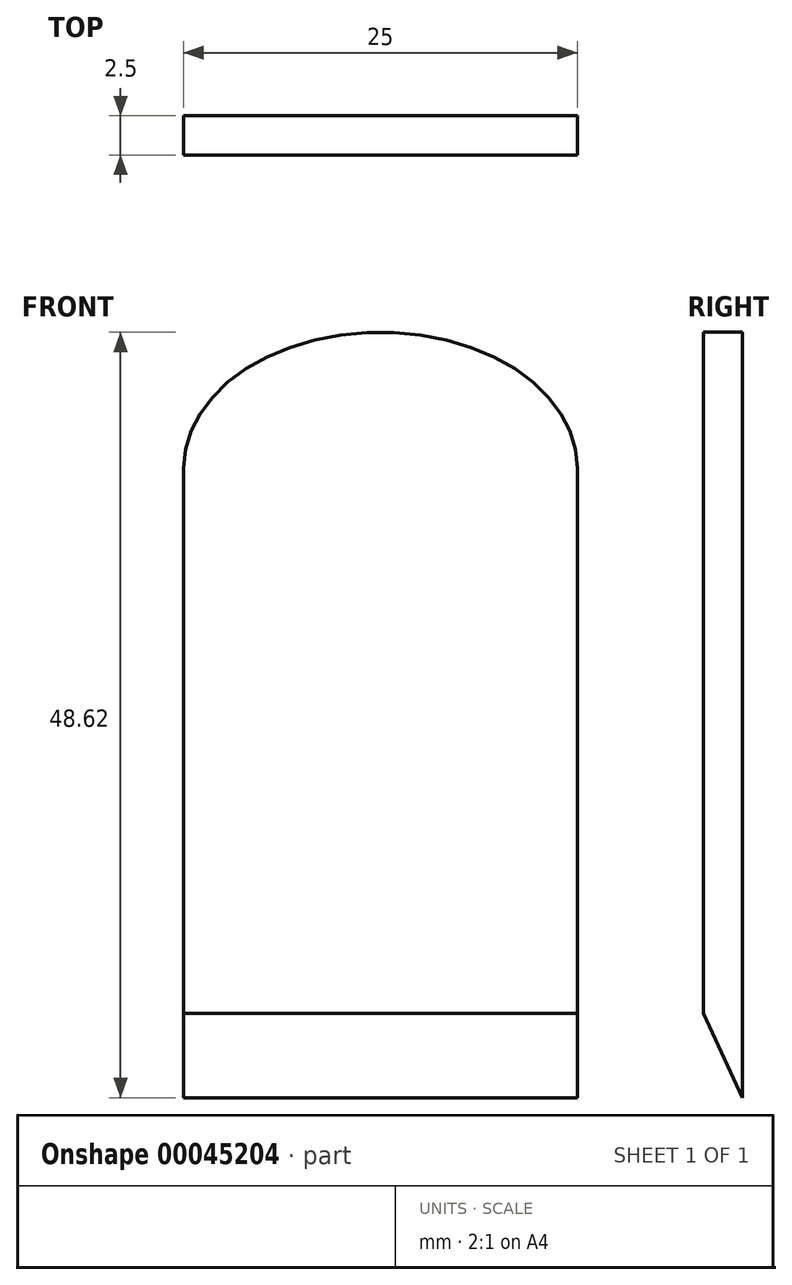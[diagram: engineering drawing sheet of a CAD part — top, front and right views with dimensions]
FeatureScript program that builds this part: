
annotation { "Feature Type Name" : "Feature", "Feature Type Description" : "" }
export const myFeature = defineFeature(function(context is Context, id is Id, definition is map)
    precondition{}
    {
        {
            var Q0;
            Q0=qCreatedBy(makeId("Front.planeOp"),FACE);
            var sketch = newSketch(context, id + "F0", { "sketchPlane" : qUnion([Q0])});
            skLineSegment(sketch, "E0.top", {"start": v(-12.5, 0) * mm, "end": v(12.5, 0) * mm});
            skLineSegment(sketch, "E0.left", {"start": v(-12.5, 40) * mm, "end": v(-12.5, 0) * mm});
            skLineSegment(sketch, "E0.right", {"start": v(12.5, 40) * mm, "end": v(12.5, 0) * mm});
            skEllipticalArc(sketch, "E1", {});
            const initialGuessF0  = {"E1": [0, 0.04, 1, 0, 0.0125, 0.008624240866126344, 0, 3.141592653589793]};
            skSetInitialGuess(sketch, initialGuessF0);
            skSolve(sketch);
        }
        {
            var Q0;
            Q0=makeQuery(id+"F0.imprint","IMPRINT",FACE,{"disambiguationData":[TD([[makeQuery(id+"F0.imprint","IMPRINT",EDGE,{"derivedFrom":sQuery(id+"F0.wireOp",EDGE,"E0.top")}),1.0]])]});
            extrude(context, id + "F1", {"entities" : qUnion([Q0]), "depth" : 2.5 * mm});
        }
        {
            var Q0;
            Q0=makeQuery(id+"F1.opExtrude","SWEPT_FACE",FACE,{"disambiguationData":[OSD([sQuery(id+"F0.wireOp",EDGE,"E0.right")])]});
            var sketch = newSketch(context, id + "F2", { "sketchPlane" : qUnion([Q0])});
            skLineSegment(sketch, "E2", {"start": v(0, 0) * mm, "end": v(-2.5, 5.36) * mm});
            skSolve(sketch);
        }
        {
            var Q0;
            {var subQ2=sQuery(id+"F2.wireOp",EDGE,"E2");Q0=makeQuery(id+"F2.imprint","IMPRINT",FACE,{"disambiguationData":[TD([[makeQuery(id+"F2.imprint","IMPRINT",EDGE,{"derivedFrom":subQ2}),1.0]])]});}
            extrude(context, id + "F3", {"entities" : qUnion([Q0]), "operationType" : NewBodyOperationType.REMOVE, "oppositeDirection" : true, "depth" : 25 * mm});
        }
    });
